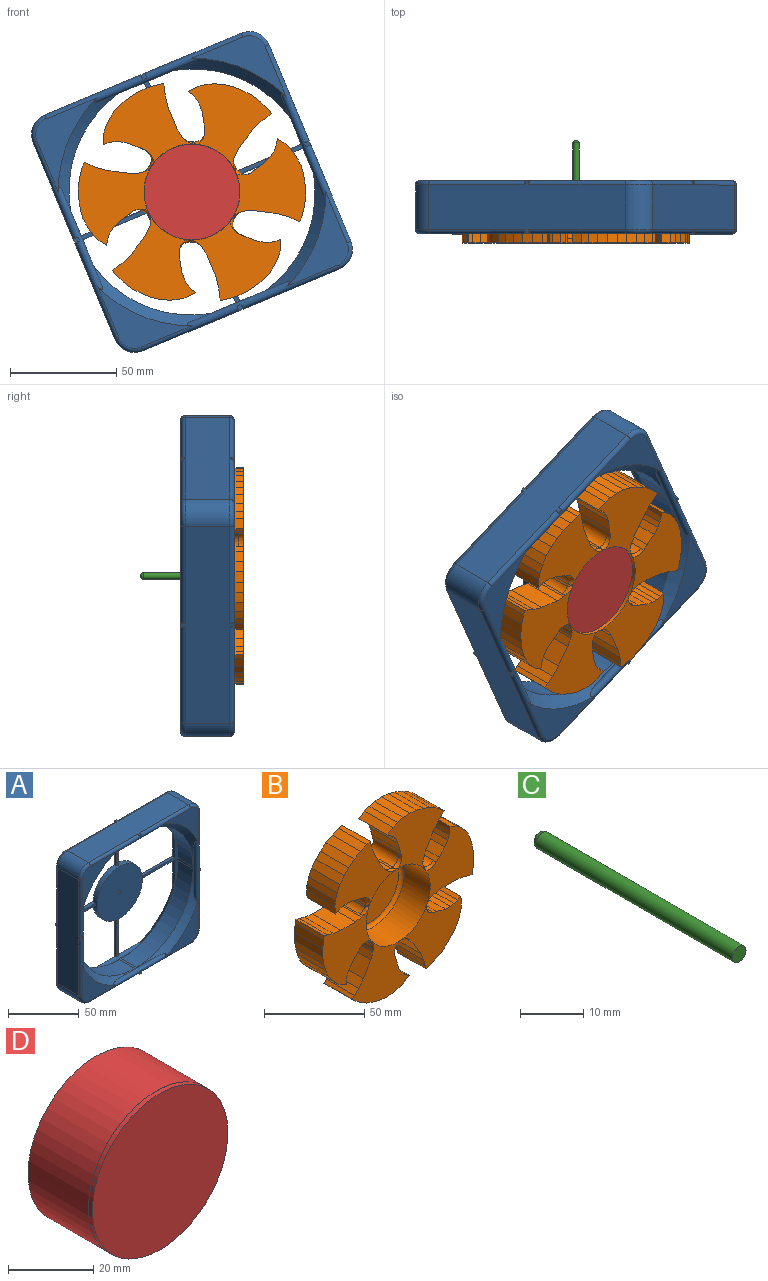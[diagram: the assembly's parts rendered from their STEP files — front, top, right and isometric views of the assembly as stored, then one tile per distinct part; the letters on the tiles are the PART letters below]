
ASSEMBLY  parts=4 mates=2
PART A: 160 faces, bbox 125x25x125 mm
  f0: plane 0.83x0.8mm, normal (0,-1,0), area 0mm2, adj f45,f46,f47,f48,f49,f54
  f1: plane 0.35x0.05mm, normal (0,-1,0), area 0mm2, adj f50,f54
  f2: plane 0.35x0.05mm, normal (0,-1,0), area 0mm2, adj f51,f54
  f3: plane 0.83x0.8mm, normal (0,-1,0), area 0mm2, adj f26,f27,f28,f52,f53,f54
  f4: plane 0.35x0.05mm, normal (0,-1,0), area 0mm2, adj f29,f54
  f5: plane 0.35x0.05mm, normal (0,-1,0), area 0mm2, adj f30,f54
  f6: plane 0.83x0.8mm, normal (0,-1,0), area 0mm2, adj f31,f32,f33,f34,f35,f54
  f7: plane 0.35x0.05mm, normal (0,-1,0), area 0mm2, adj f36,f54
  f8: plane 0.35x0.05mm, normal (0,-1,0), area 0mm2, adj f37,f54
  f9: plane 0.35x0.05mm, normal (0,-1,0), area 0mm2, adj f44,f54
  f10: plane 0.83x0.8mm, normal (0,-1,0), area 0mm2, adj f38,f39,f40,f41,f42,f54
  f11: plane 0.35x0.05mm, normal (0,-1,0), area 0mm2, adj f43,f54
  f12: cylinder r=22.5mm len=45mm, axis (0,1,0), area 587.9mm2, adj f13,f14,f15,f16,f17,f18,f19,f20
  f13: plane 120x120mm, normal (0,1,0), area 1885.7mm2, adj f12,f15,f16,f18,f19,f21,f22,f24
  f14: plane 33.59x2.01mm, normal (0,-1,0), area 67.1mm2, adj f12,f15,f16,f56
  f15: plane 35.02x2.5mm, normal (1,0,0), area 84.7mm2, adj f12,f13,f14,f56,f115
  f16: plane 35.02x2.5mm, normal (-1,0,0), area 84.7mm2, adj f12,f13,f14,f56,f116
  f17: plane 33.59x2.01mm, normal (0,-1,0), area 67.1mm2, adj f12,f18,f19,f57
  f18: plane 35.02x2.5mm, normal (0,0,-1), area 84.7mm2, adj f12,f13,f17,f57,f159
  f19: plane 35.02x2.5mm, normal (0,0,1), area 84.7mm2, adj f12,f13,f17,f57,f156
  f20: plane 33.59x2.01mm, normal (0,-1,0), area 67.1mm2, adj f12,f21,f22,f58
  f21: plane 35.02x2.5mm, normal (1,0,0), area 84.7mm2, adj f12,f13,f20,f58,f128
  f22: plane 35.02x2.5mm, normal (-1,0,0), area 84.7mm2, adj f12,f13,f20,f58,f131
  f23: plane 33.59x2.01mm, normal (0,-1,0), area 67.1mm2, adj f12,f24,f25,f59
  f24: plane 35.02x2.5mm, normal (0,0,1), area 84.7mm2, adj f12,f13,f23,f59,f143
  f25: plane 35.02x2.5mm, normal (0,0,-1), area 84.7mm2, adj f12,f13,f23,f59,f144
  f26: plane 2.5x0mm, normal (0,0,1), area 0mm2, adj f3,f13,f27,f53
  f27: plane 2.5x0.01mm, normal (0.7,0,-0.71), area 0mm2, adj f3,f13,f26,f28
  f28: plane 2.5x0.4mm, normal (0.45,0,-0.89), area 1.1mm2, adj f3,f13,f27,f29
  f29: plane 2.5x0.35mm, normal (0.14,0,-0.99), area 0.9mm2, adj f4,f13,f28,f30
  f30: plane 2.5x0.35mm, normal (-0.14,0,-0.99), area 0.9mm2, adj f5,f13,f29,f54
  f31: plane 2.5x0.35mm, normal (-0.47,0,-0.88), area 1mm2, adj f6,f13,f32,f54
  f32: plane 2.5x0.24mm, normal (-0.71,0,-0.7), area 0.8mm2, adj f6,f13,f31,f33
  f33: plane 2.5x0mm, normal (1,0,0), area 0mm2, adj f6,f13,f32,f34
  f34: plane 2.5x0.01mm, normal (-0.71,0,-0.7), area 0mm2, adj f6,f13,f33,f35
  f35: plane 2.5x0.4mm, normal (-0.89,0,-0.45), area 1.1mm2, adj f6,f13,f34,f36
  f36: plane 2.5x0.35mm, normal (-0.99,0,-0.14), area 0.9mm2, adj f7,f13,f35,f37
  f37: plane 2.5x0.35mm, normal (-0.99,0,0.14), area 0.9mm2, adj f8,f13,f36,f54
  f38: plane 2.5x0.35mm, normal (-0.88,0,0.47), area 1mm2, adj f10,f13,f39,f54
  f39: plane 2.5x0.24mm, normal (-0.7,0,0.71), area 0.8mm2, adj f10,f13,f38,f40
  f40: plane 2.5x0mm, normal (0,0,-1), area 0mm2, adj f10,f13,f39,f41
  f41: plane 2.5x0.01mm, normal (-0.7,0,0.71), area 0mm2, adj f10,f13,f40,f42
  f42: plane 2.5x0.4mm, normal (-0.45,0,0.89), area 1.1mm2, adj f10,f13,f41,f43
  f43: plane 2.5x0.35mm, normal (-0.14,0,0.99), area 0.9mm2, adj f11,f13,f42,f44
  f44: plane 2.5x0.35mm, normal (0.14,0,0.99), area 0.9mm2, adj f9,f13,f43,f54
  f45: plane 2.5x0.35mm, normal (0.47,0,0.88), area 1mm2, adj f0,f13,f46,f54
  f46: plane 2.5x0.24mm, normal (0.71,0,0.7), area 0.8mm2, adj f0,f13,f45,f47
  f47: plane 2.5x0mm, normal (-1,0,0), area 0mm2, adj f0,f13,f46,f48
  f48: plane 2.5x0.01mm, normal (0.71,0,0.7), area 0mm2, adj f0,f13,f47,f49
  f49: plane 2.5x0.4mm, normal (0.89,0,0.45), area 1.1mm2, adj f0,f13,f48,f50
  f50: plane 2.5x0.35mm, normal (0.99,0,0.14), area 0.9mm2, adj f1,f13,f49,f51
  f51: plane 2.5x0.35mm, normal (0.99,0,-0.14), area 0.9mm2, adj f2,f13,f50,f54
  f52: plane 2.5x0.35mm, normal (0.88,0,-0.47), area 1mm2, adj f3,f13,f53,f54
  f53: plane 2.5x0.24mm, normal (0.7,0,-0.71), area 0.8mm2, adj f3,f13,f26,f52
  f54: cylinder r=1.25mm len=4.3mm, axis (0,1,0), area 14.7mm2, adj f0,f1,f2,f3,f4,f5,f6,f7
  f55: plane 45x45mm, normal (0,-1,0), area 1585.5mm2, adj f12,f54
  f56: cylinder r=2mm len=100mm, axis (1,0,0), area 572.7mm2, adj f14,f15,f16,f64,f65,f71,f78,f90
  f57: cylinder r=2mm len=100mm, axis (0,0,-1), area 572.7mm2, adj f17,f18,f19,f64,f80,f85,f87,f89
  f58: cylinder r=2mm len=100mm, axis (-1,0,0), area 572.7mm2, adj f20,f21,f22,f66,f75,f82,f87,f88
  f59: cylinder r=2mm len=100mm, axis (0,0,1), area 572.7mm2, adj f23,f24,f25,f65,f66,f73,f84,f88
  f60: cylinder r=2mm len=100mm, axis (0,0,1), area 578.9mm2, adj f69,f80,f85,f86,f93,f95,f97,f99
  f61: cylinder r=2mm len=100mm, axis (0,0,-1), area 578.9mm2, adj f67,f68,f73,f84,f92,f94,f96,f98
  f62: cylinder r=2mm len=100mm, axis (1,0,0), area 578.9mm2, adj f68,f75,f82,f86,f92,f93,f96,f97
  f63: cylinder r=2mm len=100mm, axis (-1,0,0), area 578.9mm2, adj f67,f69,f71,f78,f94,f95,f98,f99
  f64: plane 33.91x33.91mm, normal (0,1,0), area 404.3mm2, adj f56,f57,f91,f103
  f65: plane 33.91x33.91mm, normal (0,1,0), area 404.3mm2, adj f56,f59,f90,f102
  f66: plane 33.91x33.91mm, normal (0,1,0), area 404.3mm2, adj f58,f59,f88,f100
  f67: plane 33.91x33.91mm, normal (0,-1,0), area 404.3mm2, adj f61,f63,f94,f98
  f68: plane 33.91x33.91mm, normal (0,-1,0), area 404.3mm2, adj f61,f62,f92,f96
  f69: plane 33.91x33.91mm, normal (0,-1,0), area 404.3mm2, adj f60,f63,f95,f99
  f70: cylinder r=10mm len=21mm, axis (0,1,0), area 329.9mm2, adj f71,f85,f91,f95
  f71: plane 100x25mm, normal (0,0,-1), area 2108mm2, adj f13,f56,f63,f70,f72,f111,f112,f113
  f72: cylinder r=10mm len=21mm, axis (0,1,0), area 329.9mm2, adj f71,f73,f90,f94
  f73: plane 100x25mm, normal (1,0,0), area 2108mm2, adj f13,f59,f61,f72,f74,f136,f137,f138
  f74: cylinder r=10mm len=21mm, axis (0,1,0), area 329.9mm2, adj f73,f75,f88,f92
  f75: plane 100x25mm, normal (0,0,1), area 2108mm2, adj f13,f58,f62,f74,f76,f125,f126,f127
  f76: cylinder r=10mm len=21mm, axis (0,1,0), area 329.9mm2, adj f75,f85,f89,f93
  f77: cylinder r=56.5mm len=56.5mm, axis (0,1,0), area 1331.2mm2, adj f78,f84,f98,f102
  f78: plane 17.13x2mm, normal (0,0,1), area 34.3mm2, adj f56,f63,f77,f79,f104,f105,f106,f107
  f79: cylinder r=56.5mm len=56.5mm, axis (0,1,0), area 1331.2mm2, adj f78,f80,f99,f103
  f80: plane 17.13x2mm, normal (1,0,0), area 34.3mm2, adj f57,f60,f79,f81,f146,f147,f148,f149
  f81: cylinder r=56.5mm len=56.5mm, axis (0,1,0), area 1331.2mm2, adj f80,f82,f97,f101
  f82: plane 17.13x2mm, normal (0,0,-1), area 34.3mm2, adj f58,f62,f81,f83,f118,f119,f120,f121
  f83: cylinder r=56.5mm len=56.5mm, axis (0,1,0), area 1331.2mm2, adj f82,f84,f96,f100
  f84: plane 17.13x2mm, normal (-1,0,0), area 34.3mm2, adj f59,f61,f77,f83,f132,f133,f134,f135
  f85: plane 100x25mm, normal (-1,0,0), area 2108mm2, adj f13,f57,f60,f70,f76,f153,f154,f155
  f86: plane 33.91x33.91mm, normal (0,-1,0), area 404.3mm2, adj f60,f62,f93,f97
  f87: plane 33.91x33.91mm, normal (0,1,0), area 404.3mm2, adj f57,f58,f89,f101
  f88: torus R=8mm, axis (0,-1,0), area 45.8mm2, adj f58,f59,f66,f74
  f89: torus R=8mm, axis (0,-1,0), area 45.8mm2, adj f57,f58,f76,f87
  f90: torus R=8mm, axis (0,-1,0), area 45.8mm2, adj f56,f59,f65,f72
  f91: torus R=8mm, axis (0,-1,0), area 45.8mm2, adj f56,f57,f64,f70
  f92: torus R=8mm, axis (0,-1,0), area 45.8mm2, adj f61,f62,f68,f74
  f93: torus R=8mm, axis (0,-1,0), area 45.8mm2, adj f60,f62,f76,f86
  f94: torus R=8mm, axis (0,-1,0), area 45.8mm2, adj f61,f63,f67,f72
  f95: torus R=8mm, axis (0,-1,0), area 45.8mm2, adj f60,f63,f69,f70
  f96: cone r=56.5mm half-angle=45deg, axis (0,-1,0), area 409mm2, adj f61,f62,f68,f83,f121,f134
  f97: cone r=56.5mm half-angle=45deg, axis (0,-1,0), area 409mm2, adj f60,f62,f81,f86,f120,f149
  f98: cone r=56.5mm half-angle=45deg, axis (0,-1,0), area 409mm2, adj f61,f63,f67,f77,f106,f135
  f99: cone r=56.5mm half-angle=45deg, axis (0,-1,0), area 409mm2, adj f60,f63,f69,f79,f107,f148
  f100: cone r=61.5mm half-angle=45deg, axis (0,1,0), area 409mm2, adj f58,f59,f66,f83,f118,f133
  f101: cone r=61.5mm half-angle=45deg, axis (0,1,0), area 409mm2, adj f57,f58,f81,f87,f119,f146
  f102: cone r=61.5mm half-angle=45deg, axis (0,1,0), area 409mm2, adj f56,f59,f65,f77,f105,f132
  f103: cone r=61.5mm half-angle=45deg, axis (0,1,0), area 409mm2, adj f56,f57,f64,f79,f104,f147
  f104: plane 1.09x1.09mm, normal (-1,0,0), area 0.5mm2, adj f56,f78,f103
  f105: plane 1.09x1.09mm, normal (1,0,0), area 0.5mm2, adj f56,f78,f102
  f106: plane 1.09x1.09mm, normal (1,0,0), area 0.5mm2, adj f63,f78,f98
  f107: plane 1.09x1.09mm, normal (-1,0,0), area 0.5mm2, adj f63,f78,f99
  f108: plane 0.5x0.06mm, normal (-1,0,0), area 0mm2, adj f63,f109,f111
  f109: plane 2x0.06mm, normal (0,0,1), area 0.1mm2, adj f63,f108,f110,f111
  f110: plane 0.5x0.06mm, normal (1,0,0), area 0mm2, adj f63,f109,f111
  f111: plane 2.5x2mm, normal (0,-1,0), area 5mm2, adj f71,f108,f109,f110,f112,f113
  f112: plane 2x2mm, normal (-1,0,0), area 0.9mm2, adj f63,f71,f111
  f113: plane 2x2mm, normal (1,0,0), area 0.9mm2, adj f63,f71,f111
  f114: plane 2x2mm, normal (1,0,0), area 0.9mm2, adj f13,f56,f71
  f115: plane 0.5x0.06mm, normal (1,0,0), area 0mm2, adj f13,f15,f56
  f116: plane 0.5x0.06mm, normal (-1,0,0), area 0mm2, adj f13,f16,f56
  f117: plane 2x2mm, normal (-1,0,0), area 0.9mm2, adj f13,f56,f71
  f118: plane 1.09x1.09mm, normal (1,0,0), area 0.5mm2, adj f58,f82,f100
  f119: plane 1.09x1.09mm, normal (-1,0,0), area 0.5mm2, adj f58,f82,f101
  f120: plane 1.09x1.09mm, normal (-1,0,0), area 0.5mm2, adj f62,f82,f97
  f121: plane 1.09x1.09mm, normal (1,0,0), area 0.5mm2, adj f62,f82,f96
  f122: plane 2x0.06mm, normal (0,0,-1), area 0.1mm2, adj f62,f123,f124,f125
  f123: plane 0.5x0.06mm, normal (-1,0,0), area 0mm2, adj f62,f122,f125
  f124: plane 0.5x0.06mm, normal (1,0,0), area 0mm2, adj f62,f122,f125
  f125: plane 2.5x2mm, normal (0,-1,0), area 5mm2, adj f75,f122,f123,f124,f126,f127
  f126: plane 2x2mm, normal (1,0,0), area 0.9mm2, adj f62,f75,f125
  f127: plane 2x2mm, normal (-1,0,0), area 0.9mm2, adj f62,f75,f125
  f128: plane 0.5x0.06mm, normal (1,0,0), area 0mm2, adj f13,f21,f58
  f129: plane 2x2mm, normal (1,0,0), area 0.9mm2, adj f13,f58,f75
  f130: plane 2x2mm, normal (-1,0,0), area 0.9mm2, adj f13,f58,f75
  f131: plane 0.5x0.06mm, normal (-1,0,0), area 0mm2, adj f13,f22,f58
  f132: plane 1.09x1.09mm, normal (0,0,-1), area 0.5mm2, adj f59,f84,f102
  f133: plane 1.09x1.09mm, normal (0,0,1), area 0.5mm2, adj f59,f84,f100
  f134: plane 1.09x1.09mm, normal (0,0,1), area 0.5mm2, adj f61,f84,f96
  f135: plane 1.09x1.09mm, normal (0,0,-1), area 0.5mm2, adj f61,f84,f98
  f136: plane 2.5x2mm, normal (0,-1,0), area 5mm2, adj f73,f137,f138,f139,f140,f141
  f137: plane 2x2mm, normal (0,0,-1), area 0.9mm2, adj f61,f73,f136
  f138: plane 2x2mm, normal (0,0,1), area 0.9mm2, adj f61,f73,f136
  f139: plane 0.5x0.06mm, normal (0,0,-1), area 0mm2, adj f61,f136,f141
  f140: plane 0.5x0.06mm, normal (0,0,1), area 0mm2, adj f61,f136,f141
  f141: plane 2x0.06mm, normal (-1,0,0), area 0.1mm2, adj f61,f136,f139,f140
  f142: plane 2x2mm, normal (0,0,1), area 0.9mm2, adj f13,f59,f73
  f143: plane 0.5x0.06mm, normal (0,0,1), area 0mm2, adj f13,f24,f59
  f144: plane 0.5x0.06mm, normal (0,0,-1), area 0mm2, adj f13,f25,f59
  f145: plane 2x2mm, normal (0,0,-1), area 0.9mm2, adj f13,f59,f73
  f146: plane 1.09x1.09mm, normal (0,0,1), area 0.5mm2, adj f57,f80,f101
  f147: plane 1.09x1.09mm, normal (0,0,-1), area 0.5mm2, adj f57,f80,f103
  f148: plane 1.09x1.09mm, normal (0,0,-1), area 0.5mm2, adj f60,f80,f99
  f149: plane 1.09x1.09mm, normal (0,0,1), area 0.5mm2, adj f60,f80,f97
  f150: plane 0.5x0.06mm, normal (0,0,1), area 0mm2, adj f60,f151,f153
  f151: plane 2x0.06mm, normal (1,0,0), area 0.1mm2, adj f60,f150,f152,f153
  f152: plane 0.5x0.06mm, normal (0,0,-1), area 0mm2, adj f60,f151,f153
  f153: plane 2.5x2mm, normal (0,-1,0), area 5mm2, adj f85,f150,f151,f152,f154,f155
  f154: plane 2x2mm, normal (0,0,1), area 0.9mm2, adj f60,f85,f153
  f155: plane 2x2mm, normal (0,0,-1), area 0.9mm2, adj f60,f85,f153
  f156: plane 0.5x0.06mm, normal (0,0,1), area 0mm2, adj f13,f19,f57
  f157: plane 2x2mm, normal (0,0,1), area 0.9mm2, adj f13,f57,f85
  f158: plane 2x2mm, normal (0,0,-1), area 0.9mm2, adj f13,f57,f85
  f159: plane 0.5x0.06mm, normal (0,0,-1), area 0mm2, adj f13,f18,f57
PART B: 180 faces, bbox 106.4x27.9x104.2 mm
  f0: plane 42.18x37.41mm, normal (0,-1,0), area 789.2mm2, adj f5,f6,f7,f8,f9,f10,f11,f12
  f1: plane 40.02x38.78mm, normal (0,-1,0), area 789.2mm2, adj f120,f121,f122,f123,f124,f125,f126,f127
  f2: plane 39x33.64mm, normal (0,-1,0), area 789.2mm2, adj f97,f98,f99,f100,f101,f102,f103,f104
  f3: plane 42.18x37.41mm, normal (0,-1,0), area 789.2mm2, adj f74,f75,f76,f77,f78,f79,f80,f81
  f4: plane 40.02x38.78mm, normal (0,-1,0), area 789.2mm2, adj f51,f52,f53,f54,f55,f56,f57,f58
  f5: plane 20x1.07mm, normal (-0.67,0,-0.74), area 21.2mm2, adj f0,f6,f145,f176,f178
  f6: plane 20x3.3mm, normal (-0.77,0,-0.64), area 85.8mm2, adj f0,f5,f7,f145
  f7: plane 20x8.99mm, normal (-0.87,0,-0.5), area 207.6mm2, adj f0,f6,f8,f145
  f8: plane 20x5.07mm, normal (-0.93,0,-0.38), area 109.6mm2, adj f0,f7,f9,f145
  f9: plane 20x3.93mm, normal (-0.97,0,-0.24), area 81.1mm2, adj f0,f8,f10,f145
  f10: plane 20x2.23mm, normal (-0.96,0,-0.28), area 46.5mm2, adj f0,f9,f11,f145
  f11: plane 20x2.37mm, normal (0.28,0,-0.96), area 49.3mm2, adj f0,f10,f12,f145
  f12: plane 20x4.53mm, normal (0.4,0,-0.92), area 98.8mm2, adj f0,f11,f13,f145
  f13: plane 20x4.31mm, normal (0.5,0,-0.87), area 99.6mm2, adj f0,f12,f14,f145
  f14: plane 20x3.86mm, normal (0.64,0,-0.76), area 101.1mm2, adj f0,f13,f15,f145
  f15: plane 20x3.28mm, normal (0.71,0,-0.7), area 92.2mm2, adj f0,f14,f16,f145
  f16: plane 20x3.88mm, normal (0.79,0,-0.61), area 98mm2, adj f0,f15,f17,f145
  f17: plane 20x4.33mm, normal (0.91,0,-0.41), area 95mm2, adj f0,f16,f18,f145
  f18: plane 20x4mm, normal (0.95,0,-0.3), area 83.9mm2, adj f0,f17,f19,f145
  f19: plane 20x3.34mm, normal (0.99,0,-0.12), area 67.3mm2, adj f0,f18,f20,f145
  f20: plane 20x4.84mm, normal (1,0,0.1), area 97.3mm2, adj f0,f19,f21,f145
  f21: plane 20x2.12mm, normal (-0.5,0,0.87), area 48.9mm2, adj f0,f20,f22,f145
  f22: plane 20x2.62mm, normal (-0.32,0,0.95), area 55.4mm2, adj f0,f21,f23,f145
  f23: plane 20x2.65mm, normal (-0.12,0,0.99), area 53.5mm2, adj f0,f22,f24,f145
  f24: plane 20x3.75mm, normal (0.06,0,1), area 75.1mm2, adj f0,f23,f25,f145
  f25: plane 20x5.73mm, normal (0.24,0,0.97), area 117.9mm2, adj f0,f24,f26,f145
  f26: plane 20x3.01mm, normal (0.27,0,0.96), area 56.6mm2, adj f0,f25,f145,f157,f159
  f27: cylinder r=23.53mm len=18mm, axis (0,1,0), area 19.8mm2, adj f145,f155,f156,f157
  f28: plane 20x1.36mm, normal (0.31,0,-0.95), area 21.2mm2, adj f29,f144,f145,f156,f158
  f29: plane 20x4.23mm, normal (0.17,0,-0.99), area 85.8mm2, adj f28,f30,f144,f145
  f30: plane 20x10.38mm, normal (0,0,-1), area 207.6mm2, adj f29,f31,f144,f145
  f31: plane 20x5.43mm, normal (-0.13,0,-0.99), area 109.6mm2, adj f30,f32,f144,f145
  f32: plane 20x3.9mm, normal (-0.27,0,-0.96), area 81.1mm2, adj f31,f33,f144,f145
  f33: plane 20x2.26mm, normal (-0.24,0,-0.97), area 46.5mm2, adj f32,f34,f144,f145
  f34: plane 20x2.4mm, normal (0.97,0,-0.24), area 49.3mm2, adj f33,f35,f144,f145
  f35: plane 20x4.91mm, normal (0.99,0,-0.11), area 98.8mm2, adj f34,f36,f144,f145
  f36: plane 20x4.98mm, normal (1,0,0), area 99.6mm2, adj f35,f37,f144,f145
  f37: plane 20x4.97mm, normal (0.98,0,0.18), area 101.1mm2, adj f36,f38,f144,f145
  f38: plane 20x4.44mm, normal (0.96,0,0.26), area 92.2mm2, adj f37,f39,f144,f145
  f39: plane 20x4.54mm, normal (0.93,0,0.38), area 98mm2, adj f38,f40,f144,f145
  f40: plane 20x3.86mm, normal (0.81,0,0.58), area 95mm2, adj f39,f41,f144,f145
  f41: plane 20x3.09mm, normal (0.74,0,0.68), area 83.9mm2, adj f40,f42,f144,f145
  f42: plane 20x2.68mm, normal (0.6,0,0.8), area 67.3mm2, adj f41,f43,f144,f145
  f43: plane 20x4.43mm, normal (0.41,0,0.91), area 97.3mm2, adj f42,f44,f144,f145
  f44: plane 20x2.44mm, normal (-1,0,0), area 48.9mm2, adj f43,f45,f144,f145
  f45: plane 20x2.72mm, normal (-0.98,0,0.2), area 55.4mm2, adj f44,f46,f144,f145
  f46: plane 20x2.46mm, normal (-0.92,0,0.39), area 53.5mm2, adj f45,f47,f144,f145
  f47: plane 20x3.14mm, normal (-0.84,0,0.55), area 75.1mm2, adj f46,f48,f144,f145
  f48: plane 20x4.27mm, normal (-0.72,0,0.69), area 117.9mm2, adj f47,f49,f144,f145
  f49: plane 20x2.22mm, normal (-0.7,0,0.71), area 56.6mm2, adj f48,f144,f145,f161,f163
  f50: cylinder r=23.53mm len=18mm, axis (0,1,0), area 19.8mm2, adj f145,f154,f160,f161
  f51: plane 20x1.4mm, normal (0.98,0,-0.21), area 21.2mm2, adj f4,f52,f145,f160,f162
  f52: plane 20x4.03mm, normal (0.94,0,-0.34), area 85.8mm2, adj f4,f51,f53,f145
  f53: plane 20x8.99mm, normal (0.87,0,-0.5), area 207.6mm2, adj f4,f52,f54,f145
  f54: plane 20x4.34mm, normal (0.79,0,-0.61), area 109.6mm2, adj f4,f53,f55,f145
  f55: plane 20x2.91mm, normal (0.7,0,-0.72), area 81.1mm2, adj f4,f54,f56,f145
  f56: plane 20x1.68mm, normal (0.72,0,-0.69), area 46.5mm2, adj f4,f55,f57,f145
  f57: plane 20x1.78mm, normal (0.69,0,0.72), area 49.3mm2, adj f4,f56,f58,f145
  f58: plane 20x3.98mm, normal (0.59,0,0.81), area 98.8mm2, adj f4,f57,f59,f145
  f59: plane 20x4.31mm, normal (0.5,0,0.87), area 99.6mm2, adj f4,f58,f60,f145
  f60: plane 20x4.75mm, normal (0.34,0,0.94), area 101.1mm2, adj f4,f59,f61,f145
  f61: plane 20x4.46mm, normal (0.25,0,0.97), area 92.2mm2, adj f4,f60,f62,f145
  f62: plane 20x4.86mm, normal (0.13,0,0.99), area 98mm2, adj f4,f61,f63,f145
  f63: plane 20x4.73mm, normal (-0.1,0,1), area 95mm2, adj f4,f62,f64,f145
  f64: plane 20x4.09mm, normal (-0.22,0,0.98), area 83.9mm2, adj f4,f63,f65,f145
  f65: plane 20x3.1mm, normal (-0.39,0,0.92), area 67.3mm2, adj f4,f64,f66,f145
  f66: plane 20x3.96mm, normal (-0.58,0,0.81), area 97.3mm2, adj f4,f65,f67,f145
  f67: plane 20x2.12mm, normal (-0.5,0,-0.87), area 48.9mm2, adj f4,f66,f68,f145
  f68: plane 20x2.08mm, normal (-0.66,0,-0.75), area 55.4mm2, adj f4,f67,f69,f145
  f69: plane 20x2.13mm, normal (-0.8,0,-0.6), area 53.5mm2, adj f4,f68,f70,f145
  f70: plane 20x3.35mm, normal (-0.89,0,-0.45), area 75.1mm2, adj f4,f69,f71,f145
  f71: plane 20x5.66mm, normal (-0.96,0,-0.28), area 117.9mm2, adj f4,f70,f72,f145
  f72: plane 20x3.02mm, normal (-0.97,0,-0.25), area 56.6mm2, adj f4,f71,f145,f165,f167
  f73: cylinder r=23.53mm len=18mm, axis (0,1,0), area 19.8mm2, adj f145,f153,f164,f165
  f74: plane 20x1.07mm, normal (0.67,0,0.74), area 21.2mm2, adj f3,f75,f145,f164,f166
  f75: plane 20x3.3mm, normal (0.77,0,0.64), area 85.8mm2, adj f3,f74,f76,f145
  f76: plane 20x8.99mm, normal (0.87,0,0.5), area 207.6mm2, adj f3,f75,f77,f145
  f77: plane 20x5.07mm, normal (0.93,0,0.38), area 109.6mm2, adj f3,f76,f78,f145
  f78: plane 20x3.93mm, normal (0.97,0,0.24), area 81.1mm2, adj f3,f77,f79,f145
  f79: plane 20x2.23mm, normal (0.96,0,0.28), area 46.5mm2, adj f3,f78,f80,f145
  f80: plane 20x2.37mm, normal (-0.28,0,0.96), area 49.3mm2, adj f3,f79,f81,f145
  f81: plane 20x4.53mm, normal (-0.4,0,0.92), area 98.8mm2, adj f3,f80,f82,f145
  f82: plane 20x4.31mm, normal (-0.5,0,0.87), area 99.6mm2, adj f3,f81,f83,f145
  f83: plane 20x3.86mm, normal (-0.64,0,0.76), area 101.1mm2, adj f3,f82,f84,f145
  f84: plane 20x3.28mm, normal (-0.71,0,0.7), area 92.2mm2, adj f3,f83,f85,f145
  f85: plane 20x3.88mm, normal (-0.79,0,0.61), area 98mm2, adj f3,f84,f86,f145
  f86: plane 20x4.33mm, normal (-0.91,0,0.41), area 95mm2, adj f3,f85,f87,f145
  f87: plane 20x4mm, normal (-0.95,0,0.3), area 83.9mm2, adj f3,f86,f88,f145
  f88: plane 20x3.34mm, normal (-0.99,0,0.12), area 67.3mm2, adj f3,f87,f89,f145
  f89: plane 20x4.84mm, normal (-1,0,-0.1), area 97.3mm2, adj f3,f88,f90,f145
  f90: plane 20x2.12mm, normal (0.5,0,-0.87), area 48.9mm2, adj f3,f89,f91,f145
  f91: plane 20x2.62mm, normal (0.32,0,-0.95), area 55.4mm2, adj f3,f90,f92,f145
  f92: plane 20x2.65mm, normal (0.12,0,-0.99), area 53.5mm2, adj f3,f91,f93,f145
  f93: plane 20x3.75mm, normal (-0.06,0,-1), area 75.1mm2, adj f3,f92,f94,f145
  f94: plane 20x5.73mm, normal (-0.24,0,-0.97), area 117.9mm2, adj f3,f93,f95,f145
  f95: plane 20x3.01mm, normal (-0.27,0,-0.96), area 56.6mm2, adj f3,f94,f145,f169,f171
  f96: cylinder r=23.53mm len=18mm, axis (0,1,0), area 19.8mm2, adj f145,f152,f168,f169
  f97: plane 20x1.36mm, normal (-0.31,0,0.95), area 21.2mm2, adj f2,f98,f145,f168,f170
  f98: plane 20x4.23mm, normal (-0.17,0,0.99), area 85.8mm2, adj f2,f97,f99,f145
  f99: plane 20x10.38mm, normal (0,0,1), area 207.6mm2, adj f2,f98,f100,f145
  f100: plane 20x5.43mm, normal (0.13,0,0.99), area 109.6mm2, adj f2,f99,f101,f145
  f101: plane 20x3.9mm, normal (0.27,0,0.96), area 81.1mm2, adj f2,f100,f102,f145
  f102: plane 20x2.26mm, normal (0.24,0,0.97), area 46.5mm2, adj f2,f101,f103,f145
  f103: plane 20x2.4mm, normal (-0.97,0,0.24), area 49.3mm2, adj f2,f102,f104,f145
  f104: plane 20x4.91mm, normal (-0.99,0,0.11), area 98.8mm2, adj f2,f103,f105,f145
  f105: plane 20x4.98mm, normal (-1,0,0), area 99.6mm2, adj f2,f104,f106,f145
  f106: plane 20x4.97mm, normal (-0.98,0,-0.18), area 101.1mm2, adj f2,f105,f107,f145
  f107: plane 20x4.44mm, normal (-0.96,0,-0.26), area 92.2mm2, adj f2,f106,f108,f145
  f108: plane 20x4.54mm, normal (-0.93,0,-0.38), area 98mm2, adj f2,f107,f109,f145
  f109: plane 20x3.86mm, normal (-0.81,0,-0.58), area 95mm2, adj f2,f108,f110,f145
  f110: plane 20x3.09mm, normal (-0.74,0,-0.68), area 83.9mm2, adj f2,f109,f111,f145
  f111: plane 20x2.68mm, normal (-0.6,0,-0.8), area 67.3mm2, adj f2,f110,f112,f145
  f112: plane 20x4.43mm, normal (-0.41,0,-0.91), area 97.3mm2, adj f2,f111,f113,f145
  f113: plane 20x2.44mm, normal (1,0,0), area 48.9mm2, adj f2,f112,f114,f145
  f114: plane 20x2.72mm, normal (0.98,0,-0.2), area 55.4mm2, adj f2,f113,f115,f145
  f115: plane 20x2.46mm, normal (0.92,0,-0.39), area 53.5mm2, adj f2,f114,f116,f145
  f116: plane 20x3.14mm, normal (0.84,0,-0.55), area 75.1mm2, adj f2,f115,f117,f145
  f117: plane 20x4.27mm, normal (0.72,0,-0.69), area 117.9mm2, adj f2,f116,f118,f145
  f118: plane 20x2.22mm, normal (0.7,0,-0.71), area 56.6mm2, adj f2,f117,f145,f173,f175
  f119: cylinder r=23.53mm len=18mm, axis (0,1,0), area 19.8mm2, adj f145,f151,f172,f173
  f120: plane 20x1.4mm, normal (-0.98,0,0.21), area 21.2mm2, adj f1,f121,f145,f172,f174
  f121: plane 20x4.03mm, normal (-0.94,0,0.34), area 85.8mm2, adj f1,f120,f122,f145
  f122: plane 20x8.99mm, normal (-0.87,0,0.5), area 207.6mm2, adj f1,f121,f123,f145
  f123: plane 20x4.34mm, normal (-0.79,0,0.61), area 109.6mm2, adj f1,f122,f124,f145
  f124: plane 20x2.91mm, normal (-0.7,0,0.72), area 81.1mm2, adj f1,f123,f125,f145
  f125: plane 20x1.68mm, normal (-0.72,0,0.69), area 46.5mm2, adj f1,f124,f126,f145
  f126: plane 20x1.78mm, normal (-0.69,0,-0.72), area 49.3mm2, adj f1,f125,f127,f145
  f127: plane 20x3.98mm, normal (-0.59,0,-0.81), area 98.8mm2, adj f1,f126,f128,f145
  f128: plane 20x4.31mm, normal (-0.5,0,-0.87), area 99.6mm2, adj f1,f127,f129,f145
  f129: plane 20x4.75mm, normal (-0.34,0,-0.94), area 101.1mm2, adj f1,f128,f130,f145
  f130: plane 20x4.46mm, normal (-0.25,0,-0.97), area 92.2mm2, adj f1,f129,f131,f145
  f131: plane 20x4.86mm, normal (-0.13,0,-0.99), area 98mm2, adj f1,f130,f132,f145
  f132: plane 20x4.73mm, normal (0.1,0,-1), area 95mm2, adj f1,f131,f133,f145
  f133: plane 20x4.09mm, normal (0.22,0,-0.98), area 83.9mm2, adj f1,f132,f134,f145
  f134: plane 20x3.1mm, normal (0.39,0,-0.92), area 67.3mm2, adj f1,f133,f135,f145
  f135: plane 20x3.96mm, normal (0.58,0,-0.81), area 97.3mm2, adj f1,f134,f136,f145
  f136: plane 20x2.12mm, normal (0.5,0,0.87), area 48.9mm2, adj f1,f135,f137,f145
  f137: plane 20x2.08mm, normal (0.66,0,0.75), area 55.4mm2, adj f1,f136,f138,f145
  f138: plane 20x2.13mm, normal (0.8,0,0.6), area 53.5mm2, adj f1,f137,f139,f145
  f139: plane 20x3.35mm, normal (0.89,0,0.45), area 75.1mm2, adj f1,f138,f140,f145
  f140: plane 20x5.66mm, normal (0.96,0,0.28), area 117.9mm2, adj f1,f139,f141,f145
  f141: plane 20x3.02mm, normal (0.97,0,0.25), area 56.6mm2, adj f1,f140,f145,f177,f179
  f142: cylinder r=23.53mm len=18mm, axis (0,1,0), area 19.8mm2, adj f145,f150,f176,f177
  f143: cylinder r=22.55mm len=45.1mm, axis (0,1,0), area 2548.4mm2, adj f0,f1,f2,f3,f4,f144,f149,f158
  f144: plane 39x33.64mm, normal (0,-1,0), area 789.2mm2, adj f28,f29,f30,f31,f32,f33,f34,f35
  f145: plane 106.42x104.23mm, normal (0,1,0), area 4652.8mm2, adj f5,f6,f7,f8,f9,f10,f11,f12
  f146: plane 40.88x40.88mm, normal (0,1,0), area 1312.4mm2, adj f148
  f147: plane 41.1x41.1mm, normal (0,-1,0), area 1326.7mm2, adj f149
  f148: torus R=20.44mm, axis (0,-1,0), area 661.7mm2, adj f145,f146
  f149: torus R=20.55mm, axis (0,-1,0), area 430.8mm2, adj f143,f147
  f150: torus R=21.53mm, axis (0,-1,0), area 0.8mm2, adj f142,f178,f179
  f151: torus R=21.53mm, axis (0,-1,0), area 0.8mm2, adj f119,f174,f175
  f152: torus R=21.53mm, axis (0,-1,0), area 0.8mm2, adj f96,f170,f171
  f153: torus R=21.53mm, axis (0,-1,0), area 0.8mm2, adj f73,f166,f167
  f154: torus R=21.53mm, axis (0,-1,0), area 0.8mm2, adj f50,f162,f163
  f155: torus R=21.53mm, axis (0,-1,0), area 0.8mm2, adj f27,f158,f159
  f156: cylinder r=5mm len=18mm, axis (0,1,0), area 78.2mm2, adj f27,f28,f145,f158
  f157: cylinder r=5mm len=18mm, axis (0,1,0), area 156.1mm2, adj f26,f27,f145,f159
  f158: bspline ~7.14x5.44mm, area 10.7mm2, adj f28,f143,f144,f155,f156,f159
  f159: bspline ~7.86x6.91mm, area 18.7mm2, adj f0,f26,f143,f155,f157,f158
  f160: cylinder r=5mm len=18mm, axis (0,1,0), area 78.2mm2, adj f50,f51,f145,f162
  f161: cylinder r=5mm len=18mm, axis (0,1,0), area 156.1mm2, adj f49,f50,f145,f163
  f162: bspline ~7.14x6.74mm, area 10.7mm2, adj f4,f51,f143,f154,f160,f163
  f163: bspline ~8.42x7.86mm, area 18.7mm2, adj f49,f143,f144,f154,f161,f162
  f164: cylinder r=5mm len=18mm, axis (0,1,0), area 78.2mm2, adj f73,f74,f145,f166
  f165: cylinder r=5mm len=18mm, axis (0,1,0), area 156.1mm2, adj f72,f73,f145,f167
  f166: bspline ~7.14x6.67mm, area 10.7mm2, adj f3,f74,f143,f153,f164,f167
  f167: bspline ~7.86x7.81mm, area 18.7mm2, adj f4,f72,f143,f153,f165,f166
  f168: cylinder r=5mm len=18mm, axis (0,1,0), area 78.2mm2, adj f96,f97,f145,f170
  f169: cylinder r=5mm len=18mm, axis (0,1,0), area 156.1mm2, adj f95,f96,f145,f171
  f170: bspline ~7.14x5.44mm, area 10.7mm2, adj f2,f97,f143,f152,f168,f171
  f171: bspline ~7.86x6.91mm, area 18.7mm2, adj f3,f95,f143,f152,f169,f170
  f172: cylinder r=5mm len=18mm, axis (0,1,0), area 78.2mm2, adj f119,f120,f145,f174
  f173: cylinder r=5mm len=18mm, axis (0,1,0), area 156.1mm2, adj f118,f119,f145,f175
  f174: bspline ~7.14x6.74mm, area 10.7mm2, adj f1,f120,f143,f151,f172,f175
  f175: bspline ~8.42x7.86mm, area 18.7mm2, adj f2,f118,f143,f151,f173,f174
  f176: cylinder r=5mm len=18mm, axis (0,1,0), area 78.2mm2, adj f5,f142,f145,f178
  f177: cylinder r=5mm len=18mm, axis (0,1,0), area 156.1mm2, adj f141,f142,f145,f179
  f178: bspline ~7.14x6.67mm, area 10.7mm2, adj f0,f5,f143,f150,f176,f179
  f179: bspline ~7.86x7.81mm, area 18.7mm2, adj f1,f141,f143,f150,f177,f178
PART C: 4 faces, bbox 3x45.1x3 mm
  f0: cylinder r=1.5mm len=44.1mm, axis (0,-1,0), area 415.6mm2, adj f2,f3
  f1: plane 1x1mm, normal (0,1,0), area 0.8mm2, adj f3
  f2: plane 3x3mm, normal (0,-1,0), area 7.1mm2, adj f0
  f3: torus R=0.5mm, axis (0,1,0), area 11.2mm2, adj f0,f1
PART D: 7 faces, bbox 45x21.3x45 mm
  f0: cylinder r=22.47mm len=44.94mm, axis (0,1,0), area 183.5mm2, adj f1,f4
  f1: plane 44.94x44.94mm, normal (0,-1,0), area 1586.3mm2, adj f0
  f2: cylinder r=20.8mm len=41.6mm, axis (0,1,0), area 2457mm2, adj f5,f6
  f3: cylinder r=22.5mm len=45mm, axis (0,1,0), area 2827.4mm2, adj f4,f5
  f4: plane 45x45mm, normal (0,-1,0), area 4.1mm2, adj f0,f3
  f5: plane 45x45mm, normal (0,1,0), area 231.3mm2, adj f2,f3
  f6: plane 41.6x41.6mm, normal (0,1,0), area 1359.2mm2, adj f2
PLACE A rot(axis=(0,-1,0),22.6deg) t=(109.7,60.82,68.67)mm fixed
PLACE B rot(axis=(0,1,0),67.4deg) t=(109.7,51.57,68.67)mm
PLACE C rot(axis=(0,-1,0),22.6deg) t=(109.7,54.57,68.67)mm
PLACE D rot(axis=(0,-1,0),22.6deg) t=(109.7,54.57,68.67)mm
MATE revolute B.f148 <-> D.f3  axis (0,1,0) through (109.7,54.57,68.67)mm
MATE pin_slot C.f0 <-> A.f54  axis (0,-1,0) through (109.7,56.52,68.67)mm
